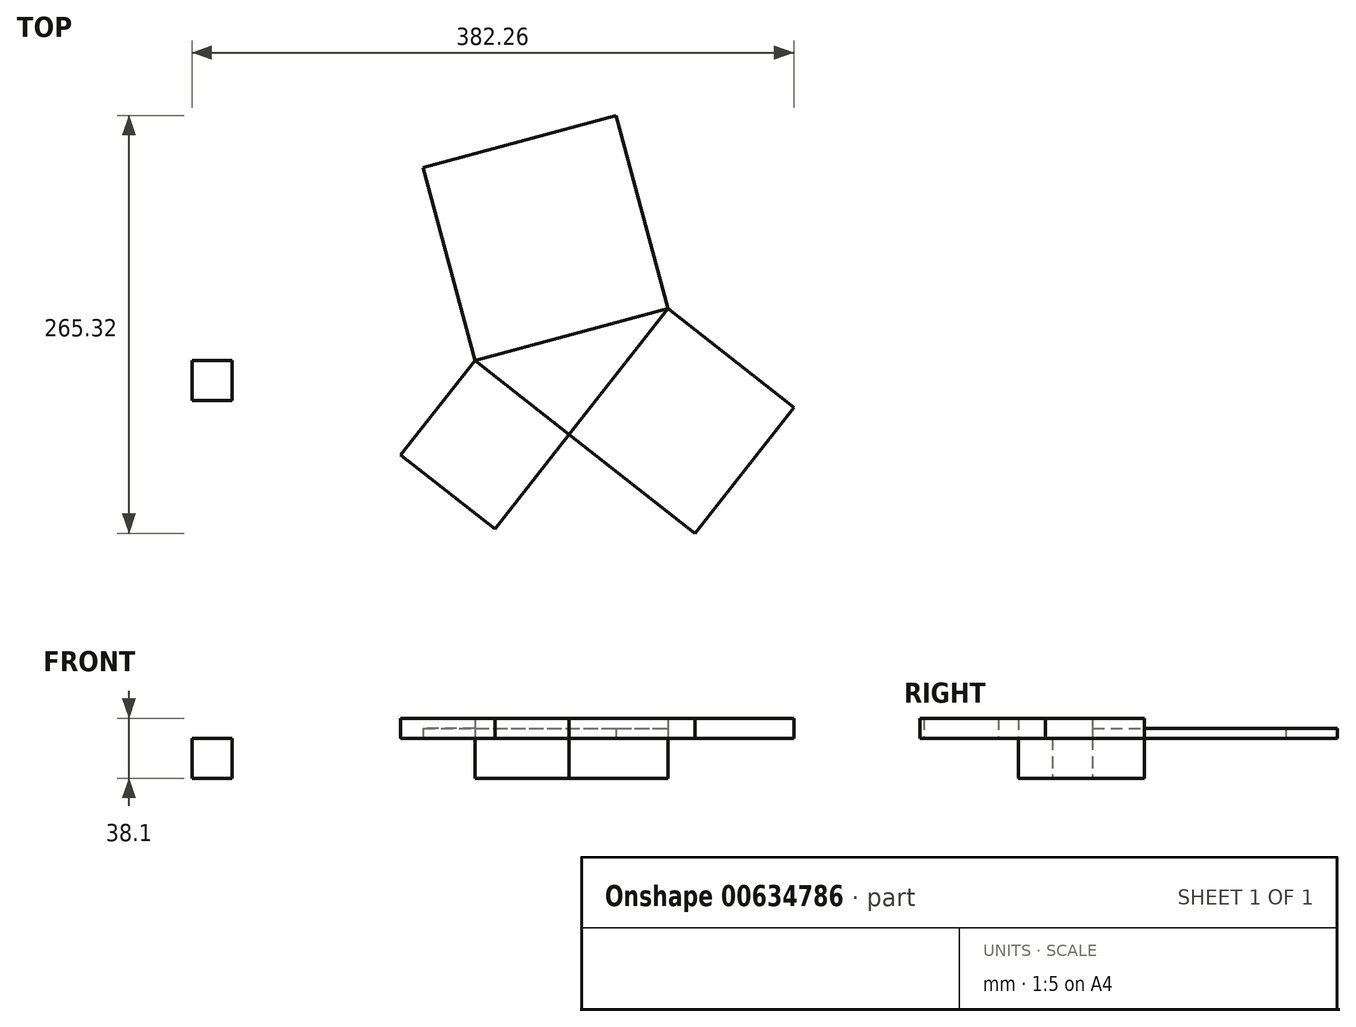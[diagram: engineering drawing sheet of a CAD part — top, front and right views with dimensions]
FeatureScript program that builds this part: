
annotation { "Feature Type Name" : "Feature", "Feature Type Description" : "" }
export const myFeature = defineFeature(function(context is Context, id is Id, definition is map)
    precondition{}
    {
        {
            var Q0;
            Q0=qCreatedBy(makeId("Top.planeOp"),FACE);
            var sketch = newSketch(context, id + "F0", { "sketchPlane" : qUnion([Q0])});
            skLineSegment(sketch, "E0.0", {"start": v(78.68, 32.87) * mm, "end": v(15.95, -47.05) * mm});
            skLineSegment(sketch, "E0.1", {"start": v(15.95, -47.05) * mm, "end": v(-44, 0) * mm});
            skLineSegment(sketch, "E0.2", {"start": v(-44, 0) * mm, "end": v(78.68, 32.87) * mm});
            skPoint(sketch, "E0.0.midPoint", {"position": v(47.31, -7.09) * mm});
            skSolve(sketch);
        }
        {
            var Q0;
            Q0=makeQuery(id+"F0.imprint","IMPRINT",FACE,{"disambiguationData":[TD([[makeQuery(id+"F0.imprint","IMPRINT",EDGE,{"derivedFrom":sQuery(id+"F0.wireOp",EDGE,"E0.0")}),-1.0]])]});
            extrude(context, id + "F1", {"entities" : qUnion([Q0]), "depth" : 25.4 * mm, "offsetDistance" : 25.4 * mm});
        }
        {
            var Q0;
            Q0=makeQuery(id+"F1.opExtrude","CAP_FACE",FACE,{"disambiguationData":[OSD([sQuery(id+"F0.wireOp",EDGE,"E0.0"),sQuery(id+"F0.wireOp",EDGE,"E0.1"),sQuery(id+"F0.wireOp",EDGE,"E0.2")])],"isStart":false});
            var sketch = newSketch(context, id + "F2", { "sketchPlane" : qUnion([Q0])});
            skLineSegment(sketch, "E1", {"start": v(-44, 0) * mm, "end": v(-91.04, -59.94) * mm});
            skLineSegment(sketch, "E2", {"start": v(-91.04, -59.94) * mm, "end": v(-31.1, -106.99) * mm});
            skLineSegment(sketch, "E3", {"start": v(-31.1, -106.99) * mm, "end": v(15.95, -47.05) * mm});
            skSolve(sketch);
        }
        {
            var Q0;
            Q0=makeQuery(id+"F2.imprint","IMPRINT",FACE,{"disambiguationData":[TD([[makeQuery(id+"F2.imprint","IMPRINT",EDGE,{"derivedFrom":makeQuery(id+"F1.opExtrude","CAP_EDGE",EDGE,{"disambiguationData":[OSD([sQuery(id+"F0.wireOp",EDGE,"E0.0")])],"isStart":false})}),-1.0]])]});
            var sketch = newSketch(context, id + "F3", { "sketchPlane" : qUnion([Q0])});
            skLineSegment(sketch, "E4", {"start": v(78.68, 32.87) * mm, "end": v(158.6, -29.86) * mm});
            skLineSegment(sketch, "E5", {"start": v(158.6, -29.86) * mm, "end": v(95.87, -109.78) * mm});
            skLineSegment(sketch, "E6", {"start": v(95.87, -109.78) * mm, "end": v(15.95, -47.05) * mm});
            skSolve(sketch);
        }
        {
            var Q0;
            Q0=makeQuery(id+"F2.imprint","IMPRINT",FACE,{"disambiguationData":[TD([[makeQuery(id+"F2.imprint","IMPRINT",EDGE,{"derivedFrom":sQuery(id+"F2.wireOp",EDGE,"E1")}),1.0]])]});
            var Q1;
            Q1=makeQuery(id+"F3.imprint","IMPRINT",FACE,{"disambiguationData":[TD([[makeQuery(id+"F3.imprint","IMPRINT",EDGE,{"derivedFrom":sQuery(id+"F3.wireOp",EDGE,"E4")}),-1.0]])]});
            extrude(context, id + "F4", {"entities" : qUnion([Q0, Q1]), "depth" : 12.7 * mm, "offsetDistance" : 25.4 * mm});
        }
        {
            var Q0;
            Q0=makeQuery(id+"F1.opExtrude","CAP_FACE",FACE,{"disambiguationData":[OSD([sQuery(id+"F0.wireOp",EDGE,"E0.0"),sQuery(id+"F0.wireOp",EDGE,"E0.1"),sQuery(id+"F0.wireOp",EDGE,"E0.2")])],"isStart":false});
            var sketch = newSketch(context, id + "F5", { "sketchPlane" : qUnion([Q0])});
            skLineSegment(sketch, "E7", {"start": v(-44, 0) * mm, "end": v(-76.86, 122.67) * mm});
            skLineSegment(sketch, "E8", {"start": v(-76.86, 122.67) * mm, "end": v(45.8, 155.54) * mm});
            skLineSegment(sketch, "E9", {"start": v(45.8, 155.54) * mm, "end": v(78.68, 32.87) * mm});
            skSolve(sketch);
        }
        {
            var Q0;
            Q0=makeQuery(id+"F5.imprint","IMPRINT",FACE,{"disambiguationData":[TD([[makeQuery(id+"F5.imprint","IMPRINT",EDGE,{"derivedFrom":sQuery(id+"F5.wireOp",EDGE,"E7")}),-1.0]])]});
            extrude(context, id + "F6", {"entities" : qUnion([Q0]), "depth" : 6.35 * mm, "offsetDistance" : 25.4 * mm});
        }
        {
            var Q0;
            Q0=qCreatedBy(makeId("Top.planeOp"),FACE);
            var sketch = newSketch(context, id + "F7", { "sketchPlane" : qUnion([Q0])});
            skLineSegment(sketch, "E10.bottom", {"start": v(-223.66, 0) * mm, "end": v(-198.26, 0) * mm});
            skLineSegment(sketch, "E10.top", {"start": v(-223.66, -25.4) * mm, "end": v(-198.26, -25.4) * mm});
            skLineSegment(sketch, "E10.left", {"start": v(-223.66, 0) * mm, "end": v(-223.66, -25.4) * mm});
            skLineSegment(sketch, "E10.right", {"start": v(-198.26, 0) * mm, "end": v(-198.26, -25.4) * mm});
            skSolve(sketch);
        }
        {
            var Q0;
            Q0=makeQuery(id+"F7.imprint","IMPRINT",FACE,{"disambiguationData":[TD([[makeQuery(id+"F7.imprint","IMPRINT",EDGE,{"derivedFrom":sQuery(id+"F7.wireOp",EDGE,"E10.bottom")}),-1.0]])]});
            extrude(context, id + "F8", {"entities" : qUnion([Q0]), "depth" : 25.4 * mm, "offsetDistance" : 25.4 * mm});
        }
    });
